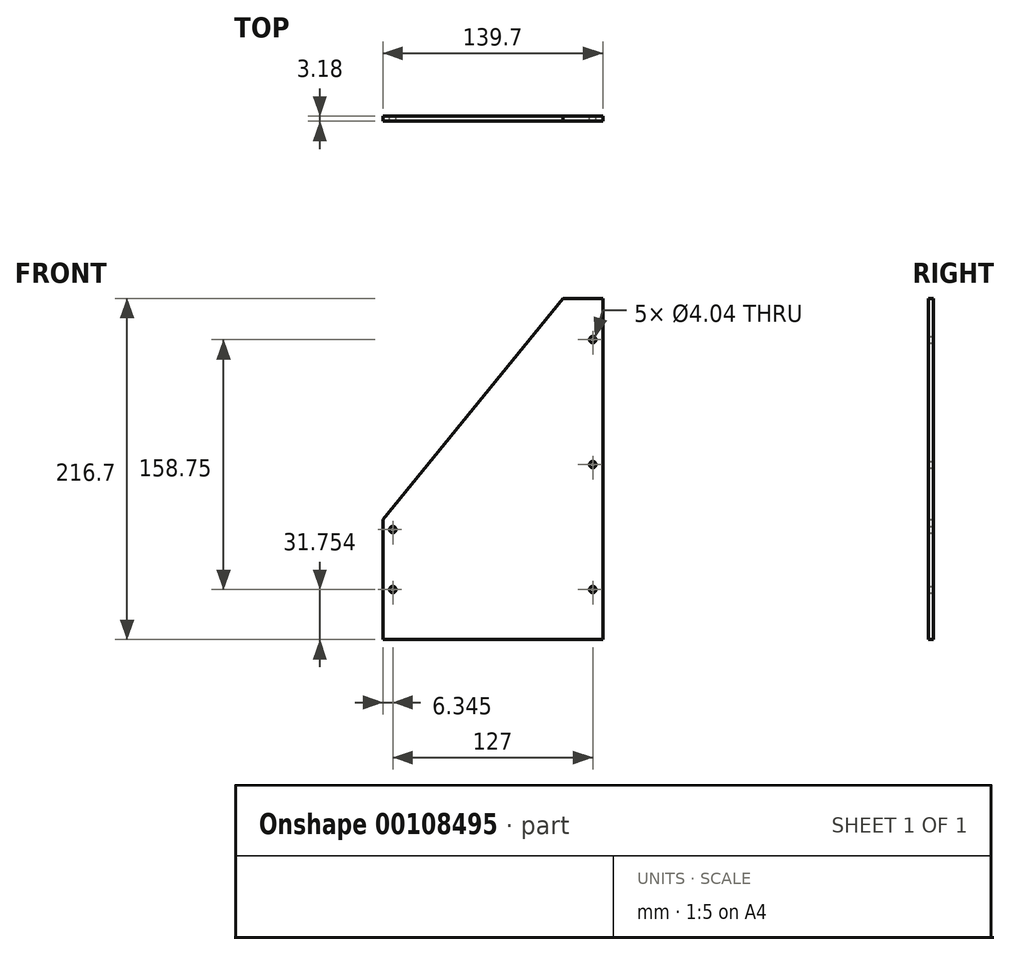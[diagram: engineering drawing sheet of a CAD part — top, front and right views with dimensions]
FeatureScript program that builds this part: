
annotation { "Feature Type Name" : "Feature", "Feature Type Description" : "" }
export const myFeature = defineFeature(function(context is Context, id is Id, definition is map)
    precondition{}
    {
        {
            var Q0;
            Q0=qCreatedBy(makeId("Front.planeOp"),FACE);
            var sketch = newSketch(context, id + "F0", { "sketchPlane" : qUnion([Q0])});
            skLineSegment(sketch, "E0", {"start": v(59.06, -94.46) * mm, "end": v(-80.64, -94.46) * mm});
            skLineSegment(sketch, "E1", {"start": v(-80.64, -94.46) * mm, "end": v(-80.64, -18.26) * mm});
            skLineSegment(sketch, "E2", {"start": v(-80.64, -18.26) * mm, "end": v(33.66, 122.24) * mm});
            skLineSegment(sketch, "E3", {"start": v(33.66, 122.24) * mm, "end": v(59.06, 122.24) * mm});
            skLineSegment(sketch, "E4", {"start": v(59.06, 122.24) * mm, "end": v(59.06, -94.46) * mm});
            skCircle(sketch, "E5", {"center": v(52.7, -62.7) * mm, "radius": 2.02 * mm});
            skCircle(sketch, "E6", {"center": v(52.7, 16.67) * mm, "radius": 2.02 * mm});
            skCircle(sketch, "E7", {"center": v(52.7, 96.04) * mm, "radius": 2.02 * mm});
            skCircle(sketch, "E8", {"center": v(-74.3, -24.6) * mm, "radius": 2.02 * mm});
            skCircle(sketch, "E9", {"center": v(-74.3, -62.7) * mm, "radius": 2.02 * mm});
            skSolve(sketch);
        }
        {
            var Q0;
            Q0=makeQuery(id+"F0.imprint","IMPRINT",FACE,{"disambiguationData":[TD([[makeQuery(id+"F0.imprint","IMPRINT",EDGE,{"derivedFrom":sQuery(id+"F0.wireOp",EDGE,"E0")}),-1.0]])]});
            extrude(context, id + "F1", {"entities" : qUnion([Q0]), "depth" : 3.17 * mm});
        }
    });
